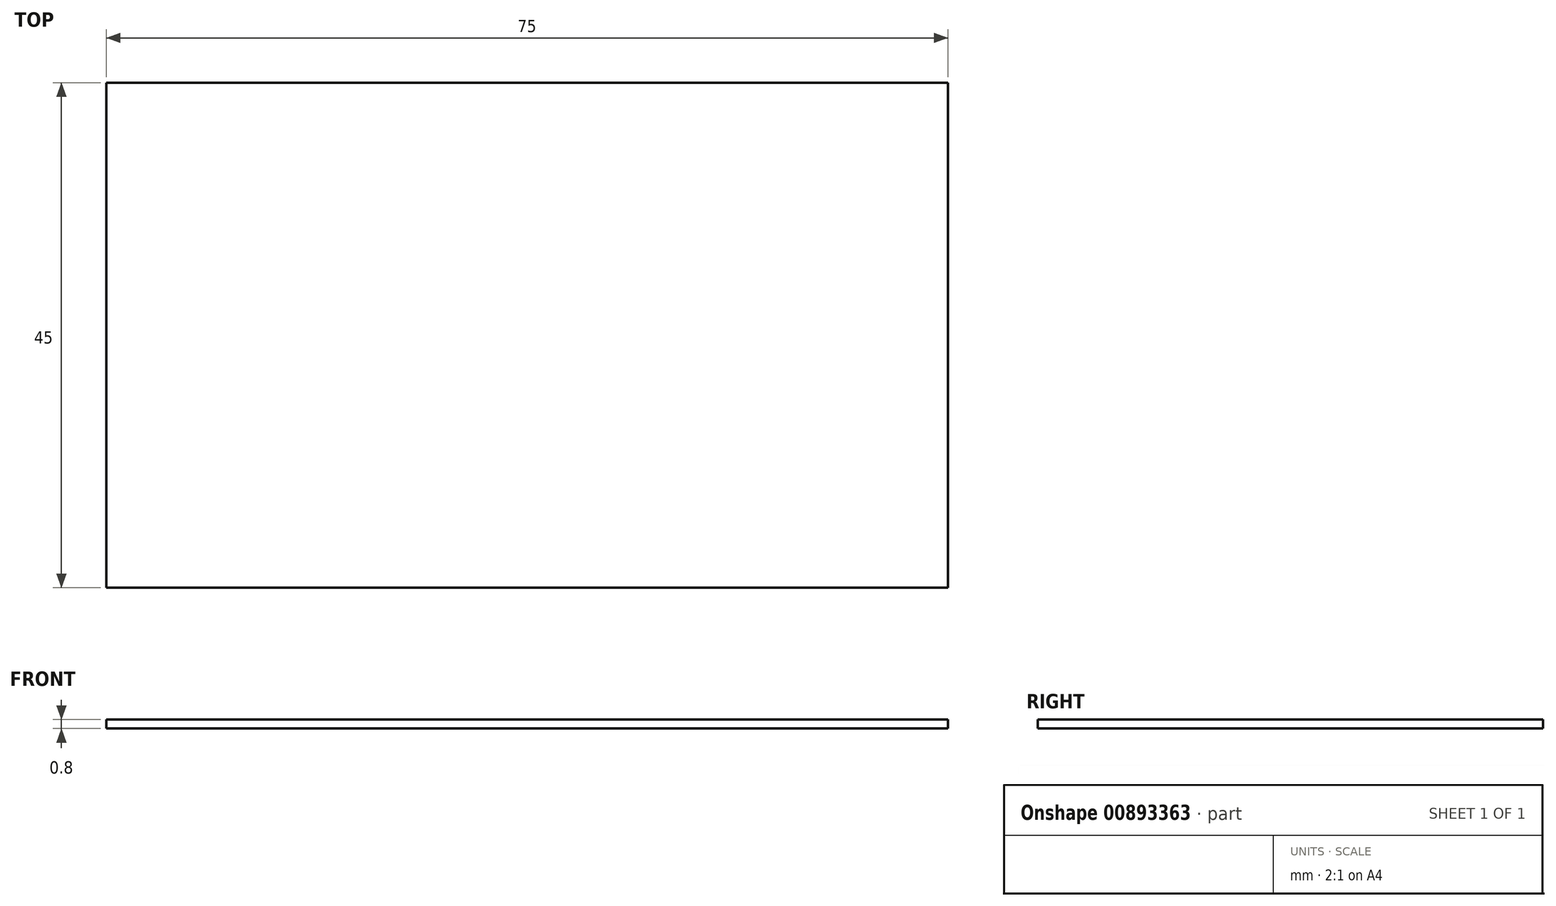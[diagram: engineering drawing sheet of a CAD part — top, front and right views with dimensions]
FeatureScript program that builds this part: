
annotation { "Feature Type Name" : "Feature", "Feature Type Description" : "" }
export const myFeature = defineFeature(function(context is Context, id is Id, definition is map)
    precondition{}
    {
        {
            var Q0;
            Q0=qCreatedBy(makeId("Top.planeOp"),FACE);
            var sketch = newSketch(context, id + "F0", { "sketchPlane" : qUnion([Q0])});
            skLineSegment(sketch, "E0.bottom", {"start": v(37.5, -22.5) * mm, "end": v(-37.5, -22.5) * mm});
            skLineSegment(sketch, "E0.top", {"start": v(37.5, 22.5) * mm, "end": v(-37.5, 22.5) * mm});
            skLineSegment(sketch, "E0.left", {"start": v(37.5, -22.5) * mm, "end": v(37.5, 22.5) * mm});
            skLineSegment(sketch, "E0.right", {"start": v(-37.5, -22.5) * mm, "end": v(-37.5, 22.5) * mm});
            skPoint(sketch, "E0.middle", {"position": v(0, 0) * mm});
            skSolve(sketch);
        }
        {
            var Q0;
            Q0=makeQuery(id+"F0.imprint","IMPRINT",FACE,{"disambiguationData":[TD([[makeQuery(id+"F0.imprint","IMPRINT",EDGE,{"derivedFrom":sQuery(id+"F0.wireOp",EDGE,"E0.bottom")}),-1.0]])]});
            extrude(context, id + "F1", {"entities" : qUnion([Q0]), "depth" : 0.8 * mm, "offsetDistance" : 25 * mm});
        }
    });
